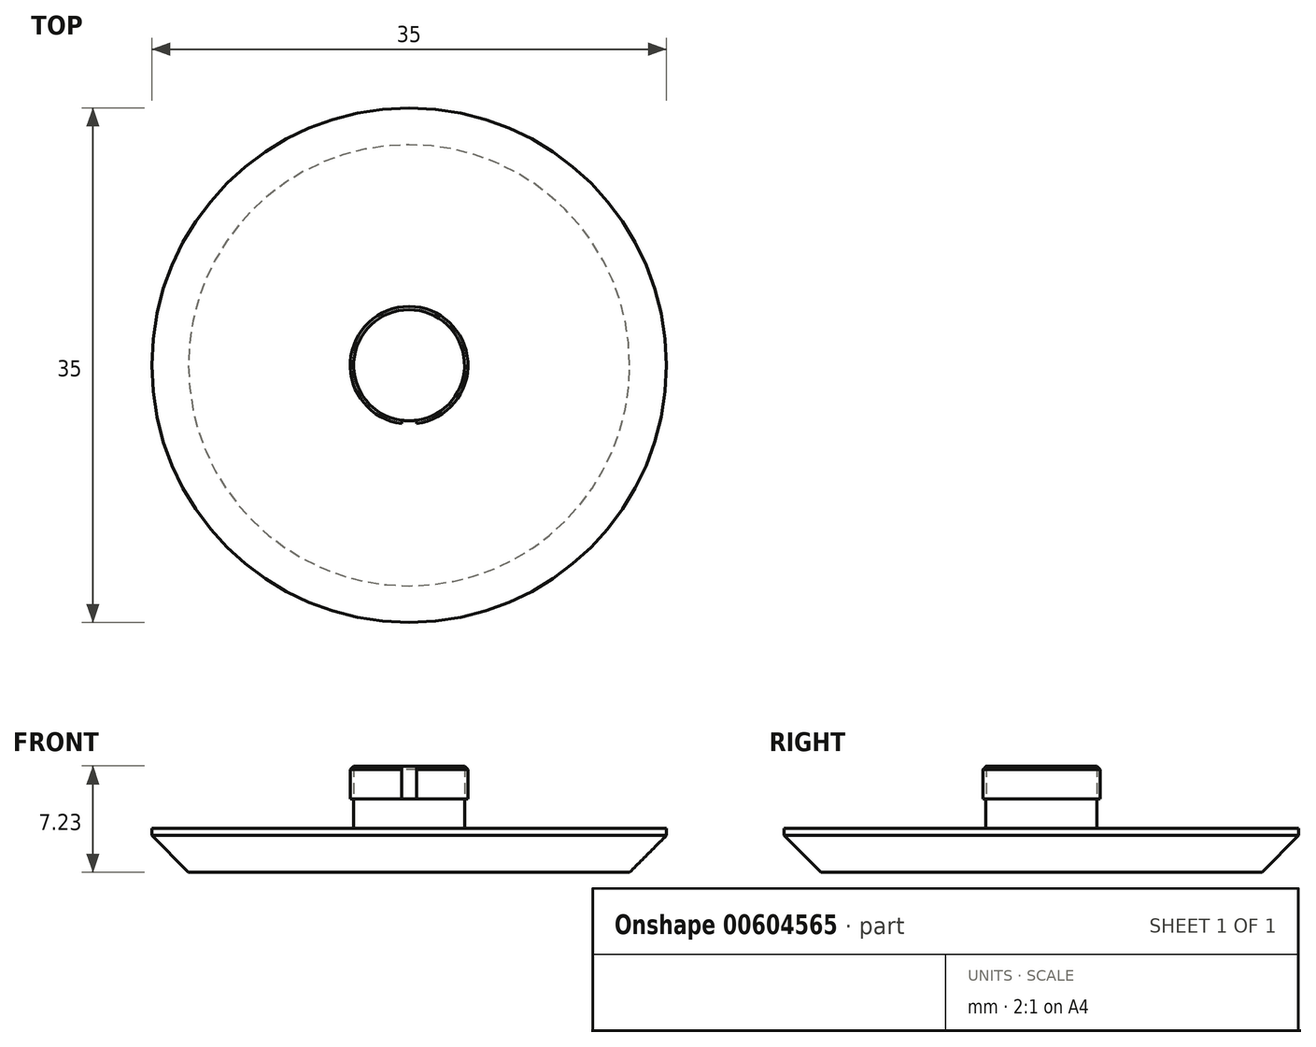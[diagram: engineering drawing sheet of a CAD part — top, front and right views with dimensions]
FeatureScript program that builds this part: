
annotation { "Feature Type Name" : "Feature", "Feature Type Description" : "" }
export const myFeature = defineFeature(function(context is Context, id is Id, definition is map)
    precondition{}
    {
        {
            var Q0;
            Q0=qCreatedBy(makeId("Top.planeOp"),FACE);
            var sketch = newSketch(context, id + "F0", { "sketchPlane" : qUnion([Q0])});
            skCircle(sketch, "E0", {"center": v(0, 0) * mm, "radius": 17.5 * mm});
            skSolve(sketch);
        }
        {
            var Q0;
            Q0 = qSketchRegion(id + "F0", true);
            extrude(context, id + "F1", {"entities" : qUnion([Q0]), "depth" : 3 * mm, "offsetDistance" : 25 * mm});
        }
        {
            var Q0;
            Q0=makeQuery(id+"F1.opExtrude","CAP_EDGE",EDGE,{"disambiguationData":[OSD([sQuery(id+"F0.wireOp",EDGE,"E0")])],"isStart":true});
            chamfer(context, id + "F2", {"entities" : qUnion([Q0]), "width" : 2.5 * mm, "tangentPropagation" : true});
        }
        {
            var Q0;
            Q0=makeQuery(id+"F1.opExtrude","CAP_FACE",FACE,{"disambiguationData":[OSD([sQuery(id+"F0.wireOp",EDGE,"E0")])],"isStart":false});
            var sketch = newSketch(context, id + "F3", { "sketchPlane" : qUnion([Q0])});
            skCircle(sketch, "E1", {"center": v(0, 0) * mm, "radius": 3.78 * mm});
            skSolve(sketch);
        }
        {
            var Q0;
            Q0 = qSketchRegion(id + "F3", true);
            extrude(context, id + "F4", {"entities" : qUnion([Q0]), "operationType" : NewBodyOperationType.ADD, "depth" : 2 * mm, "offsetDistance" : 25 * mm});
        }
        {
            var Q0;
            Q0=makeQuery(id+"F4.opExtrude","CAP_FACE",FACE,{"disambiguationData":[OSD([sQuery(id+"F3.wireOp",EDGE,"E1")])],"isStart":false});
            var sketch = newSketch(context, id + "F5", { "sketchPlane" : qUnion([Q0])});
            skCircle(sketch, "E2", {"center": v(0, 0) * mm, "radius": 4 * mm});
            skLineSegment(sketch, "E3", {"start": v(0, 3.78) * mm, "end": v(0, -3.78) * mm, "construction": true});
            skLineSegment(sketch, "E4", {"start": v(-0.5, 3.74) * mm, "end": v(-0.5, -3.74) * mm});
            skLineSegment(sketch, "E5.MirrorCS", {"start": v(0.5, 3.74) * mm, "end": v(0.5, -3.74) * mm});
            skLineSegment(sketch, "E6", {"start": v(-0.5, 3.97) * mm, "end": v(-0.5, -3.97) * mm});
            skLineSegment(sketch, "E7", {"start": v(0.5, -3.97) * mm, "end": v(0.5, 3.97) * mm});
            skSolve(sketch);
        }
        {
            var Q0;
            {var subQ0=sQuery(id+"F5.wireOp",EDGE,"E6");var subQ1=sQuery(id+"F5.wireOp",EDGE,"E2");var subQ2=makeQuery(id+"F5.imprint","INTERSECT",VERTEX,{"disambiguationData":[OD(0.0)],"derivedFrom":[subQ1,subQ0]});Q0=makeQuery(id+"F5.imprint","IMPRINT",FACE,{"disambiguationData":[TD([[makeQuery(id+"F5.imprint","IMPRINT",EDGE,{"disambiguationData":[TD([[subQ2,-1.0]])],"derivedFrom":subQ1}),1.0]])]});}
            var Q1;
            {var subQ0=sQuery(id+"F5.wireOp",EDGE,"E6");var subQ1=makeQuery(id+"F4.opExtrude","CAP_EDGE",EDGE,{"disambiguationData":[OSD([sQuery(id+"F3.wireOp",EDGE,"E1")])],"isStart":false});var subQ2=makeQuery(id+"F5.imprint","INTERSECT",VERTEX,{"disambiguationData":[OD(0.0)],"derivedFrom":[subQ1,subQ0]});Q1=makeQuery(id+"F5.imprint","IMPRINT",FACE,{"disambiguationData":[TD([[makeQuery(id+"F5.imprint","IMPRINT",EDGE,{"disambiguationData":[TD([[subQ2,-1.0]])],"derivedFrom":subQ0}),-1.0]])]});}
            var Q2;
            {var subQ0=sQuery(id+"F5.wireOp",EDGE,"E7");var subQ1=makeQuery(id+"F4.opExtrude","CAP_EDGE",EDGE,{"disambiguationData":[OSD([sQuery(id+"F3.wireOp",EDGE,"E1")])],"isStart":false});var subQ2=makeQuery(id+"F5.imprint","INTERSECT",VERTEX,{"disambiguationData":[OD(0.0)],"derivedFrom":[subQ1,subQ0]});Q2=makeQuery(id+"F5.imprint","IMPRINT",FACE,{"disambiguationData":[TD([[makeQuery(id+"F5.imprint","IMPRINT",EDGE,{"disambiguationData":[TD([[subQ2,-1.0]])],"derivedFrom":subQ0}),-1.0]])]});}
            var Q3;
            {var subQ0=sQuery(id+"F5.wireOp",EDGE,"E7");var subQ1=sQuery(id+"F5.wireOp",EDGE,"E2");var subQ2=makeQuery(id+"F5.imprint","INTERSECT",VERTEX,{"disambiguationData":[OD(0.0)],"derivedFrom":[subQ1,subQ0]});Q3=makeQuery(id+"F5.imprint","IMPRINT",FACE,{"disambiguationData":[TD([[makeQuery(id+"F5.imprint","IMPRINT",EDGE,{"disambiguationData":[TD([[subQ2,-1.0]])],"derivedFrom":subQ1}),1.0]])]});}
            extrude(context, id + "F6", {"entities" : qUnion([Q0, Q1, Q2, Q3]), "operationType" : NewBodyOperationType.ADD, "depth" : 3 * mm, "offsetDistance" : 25 * mm});
        }
        {
            var Q0;
            {var subQ0=sQuery(id+"F5.wireOp",EDGE,"E6");var subQ1=sQuery(id+"F5.wireOp",EDGE,"E2");Q0=makeQuery(id+"F6.opExtrude","CAP_EDGE",EDGE,{"disambiguationData":[OSD([subQ1]),TDD([makeQuery(id+"F5.imprint","IMPRINT",EDGE,{"disambiguationData":[TD([[makeQuery(id+"F5.imprint","INTERSECT",VERTEX,{"disambiguationData":[OD(0.0)],"derivedFrom":[subQ1,subQ0]}),-1.0]])],"derivedFrom":subQ1})])],"isStart":false});}
            var Q1;
            {var subQ0=sQuery(id+"F5.wireOp",EDGE,"E7");var subQ1=sQuery(id+"F5.wireOp",EDGE,"E2");Q1=makeQuery(id+"F6.opExtrude","CAP_EDGE",EDGE,{"disambiguationData":[OSD([subQ1]),TDD([makeQuery(id+"F5.imprint","IMPRINT",EDGE,{"disambiguationData":[TD([[makeQuery(id+"F5.imprint","INTERSECT",VERTEX,{"disambiguationData":[OD(0.0)],"derivedFrom":[subQ1,subQ0]}),-1.0]])],"derivedFrom":subQ1})])],"isStart":false});}
            chamfer(context, id + "F7", {"entities" : qUnion([Q0, Q1]), "width" : 1 * mm, "tangentPropagation" : true});
        }
    });
